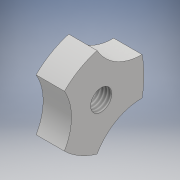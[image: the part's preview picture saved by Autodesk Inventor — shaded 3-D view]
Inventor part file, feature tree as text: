
AUTODESK INVENTOR PART (.ipt)
format: ipt  version: 2018 (Build 220112000, 112)  size: 115,200 bytes
history: native  units: mm
features: sketch x2, extrude x1, thread x1
ambient origin geometry x8: Origin, YZ Plane, XZ Plane, XY Plane, X Axis, Y Axis, Z Axis, Center Point
bodies: 实体1 (feature_tree)
feature tree (4):
  sketch  "草图1"  dims[d0=4.5mm d2=20.0mm d16=6.0mm d17=0.0mm]
  extrude  "拉伸1"  Depth=6.0mm
  thread  "螺纹1"  [1 undecoded]
  sketch  "草图2"  dims[d18=10.0mm d19=0.0mm]
note: 1 required parameter value undecoded (feature->parameter linkage not recoverable at this tier; creation-order binding heuristic only, values carry confidence <= 0.55)
